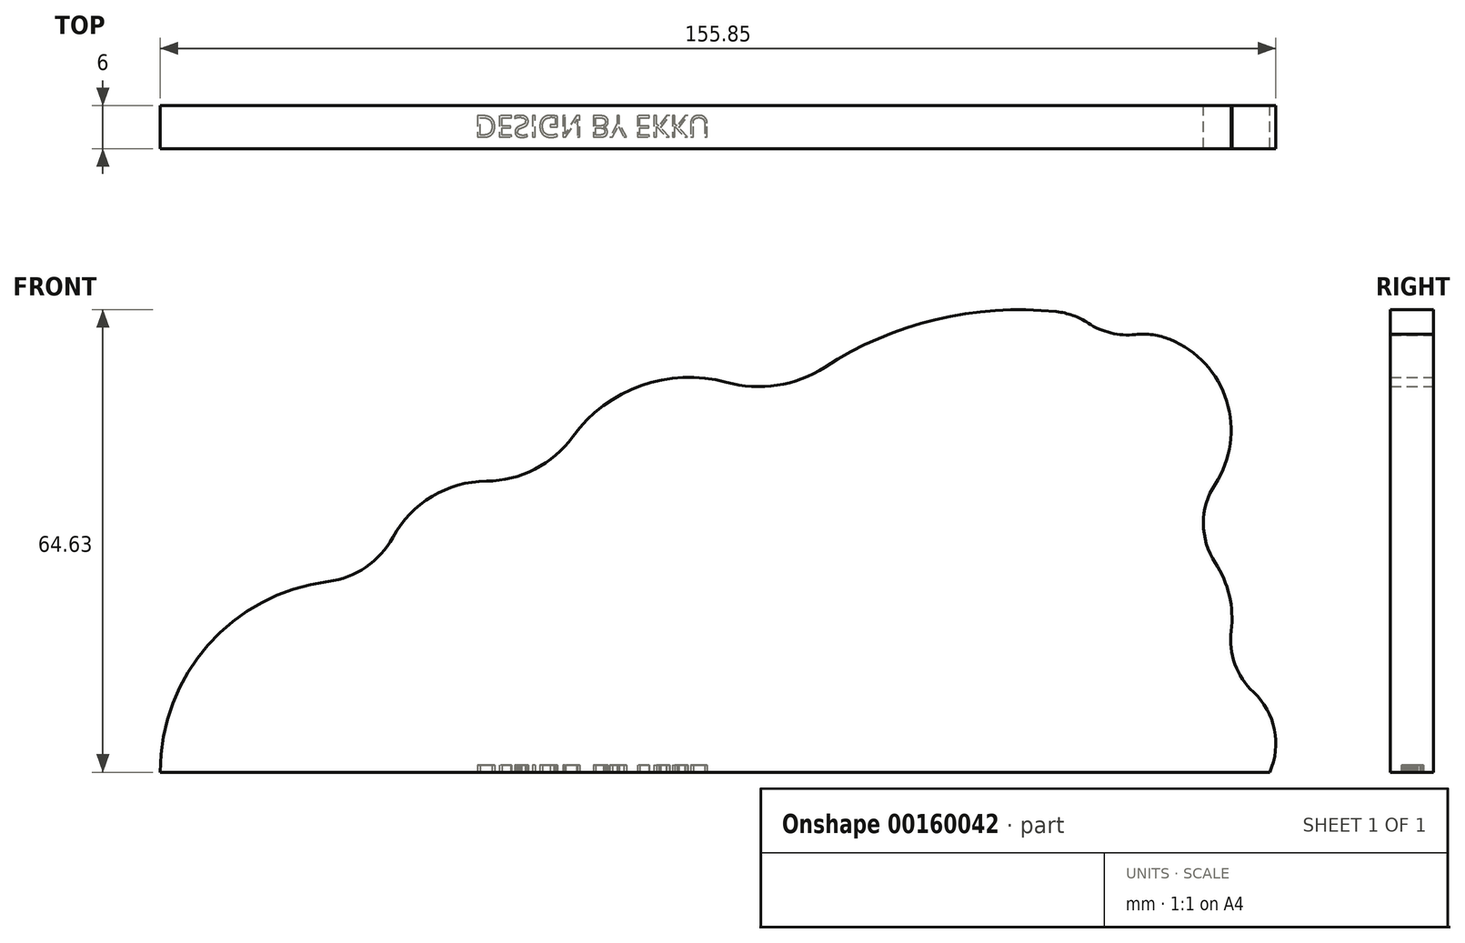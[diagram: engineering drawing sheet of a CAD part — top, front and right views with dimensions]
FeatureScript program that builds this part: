
annotation { "Feature Type Name" : "Feature", "Feature Type Description" : "" }
export const myFeature = defineFeature(function(context is Context, id is Id, definition is map)
    precondition{}
    {
        {
            var Q0;
            Q0=qCreatedBy(makeId("Front.planeOp"),FACE);
            var sketch = newSketch(context, id + "F0", { "sketchPlane" : qUnion([Q0])});
            skLineSegment(sketch, "E0", {"start": v(0, 0) * mm, "end": v(-155, 0) * mm});
            skArc(sketch, "E1", {"start": v(-109.41, 40.68) * mm, "mid": v(-117.02, 38.54) * mm, "end": v(-122.49, 32.84) * mm});
            skArc(sketch, "E2", {"start": v(-75.89, 54.47) * mm, "mid": v(-87.8, 54.04) * mm, "end": v(-97.36, 46.9) * mm});
            skArc(sketch, "E3", {"start": v(-29.82, 64.36) * mm, "mid": v(-46.66, 63.25) * mm, "end": v(-62.17, 56.6) * mm});
            skArc(sketch, "E4", {"start": v(-7.63, 40.26) * mm, "mid": v(-6, 51.86) * mm, "end": v(-13.93, 60.48) * mm});
            skArc(sketch, "E5", {"start": v(-5.38, 19.75) * mm, "mid": v(-5.64, 24.7) * mm, "end": v(-7.6, 29.26) * mm});
            skArc(sketch, "E6", {"start": v(0, 0) * mm, "mid": v(0.65, 5.96) * mm, "end": v(-2.28, 11.2) * mm});
            skArc(sketch, "E7", {"start": v(-17.22, 61.36) * mm, "mid": v(-91.43, 42.62) * mm, "end": v(-155, 0) * mm, "construction": true});
            skArc(sketch, "E8", {"start": v(-17.22, 61.36) * mm, "mid": v(-13.33, 29.35) * mm, "end": v(0, 0) * mm, "construction": true});
            skPoint(sketch, "E9.visualSharp", {"position": v(-143.88, 9.94) * mm});
            skPoint(sketch, "E10.visualSharp", {"position": v(-124.1, 23.21) * mm});
            skArc(sketch, "E10.filletArc", {"start": v(-131.52, 26.66) * mm, "mid": v(-126.26, 28.66) * mm, "end": v(-122.49, 32.84) * mm});
            skPoint(sketch, "E11.visualSharp", {"position": v(-100.93, 38.12) * mm});
            skArc(sketch, "E11.filletArc", {"start": v(-109.41, 40.68) * mm, "mid": v(-102.64, 42.34) * mm, "end": v(-97.36, 46.9) * mm});
            skPoint(sketch, "E12.visualSharp", {"position": v(-69.13, 51.16) * mm});
            skArc(sketch, "E12.filletArc", {"start": v(-75.89, 54.47) * mm, "mid": v(-68.8, 54.07) * mm, "end": v(-62.17, 56.6) * mm});
            skPoint(sketch, "E13.visualSharp", {"position": v(-14.7, 34.79) * mm});
            skArc(sketch, "E13.filletArc", {"start": v(-7.63, 40.26) * mm, "mid": v(-9.26, 34.76) * mm, "end": v(-7.6, 29.26) * mm});
            skPoint(sketch, "E14.visualSharp", {"position": v(-7.6, 13.75) * mm});
            skArc(sketch, "E14.filletArc", {"start": v(-5.38, 19.75) * mm, "mid": v(-4.86, 15.1) * mm, "end": v(-2.28, 11.2) * mm});
            skPoint(sketch, "E15.visualSharp", {"position": v(-17.22, 61.36) * mm});
            skArc(sketch, "E16", {"start": v(-25.34, 62.76) * mm, "mid": v(-22.2, 61.38) * mm, "end": v(-18.76, 61.16) * mm});
            skPoint(sketch, "E17.visualSharp", {"position": v(-26.83, 63.96) * mm});
            skArc(sketch, "E17.filletArc", {"start": v(-25.34, 62.76) * mm, "mid": v(-27.49, 63.83) * mm, "end": v(-29.82, 64.36) * mm});
            skPoint(sketch, "E18.visualSharp", {"position": v(-17.45, 61.39) * mm});
            skArc(sketch, "E18.filletArc", {"start": v(-13.93, 60.48) * mm, "mid": v(-16.3, 61.12) * mm, "end": v(-18.76, 61.16) * mm});
            skArc(sketch, "E19", {"start": v(-131.52, 26.66) * mm, "mid": v(-148.3, 17.76) * mm, "end": v(-155, 0) * mm});
            skPoint(sketch, "E20.center.orphan", {"position": v(-145, 0) * mm});
            skLineSegment(sketch, "E21", {"start": v(-155, 0) * mm, "end": v(-155, 26.27) * mm, "construction": true});
            skSolve(sketch);
        }
        {
            var Q0;
            Q0=qSketchRegion(id+"F0",true);
            extrude(context, id + "F1", {"entities" : qUnion([Q0]), "depth" : 6 * mm});
        }
        {
            var Q0;
            Q0=makeQuery(id+"F1.opExtrude","CAP_FACE",FACE,{"disambiguationData":[OSD([sQuery(id+"F0.wireOp",EDGE,"E0"),sQuery(id+"F0.wireOp",EDGE,"E20"),sQuery(id+"F0.wireOp",EDGE,"XMCz9Z54-D0iV-scBE-4L2D-qfeKU0g2q7XP"),sQuery(id+"F0.wireOp",EDGE,"E1"),sQuery(id+"F0.wireOp",EDGE,"E2"),sQuery(id+"F0.wireOp",EDGE,"E3"),sQuery(id+"F0.wireOp",EDGE,"E4"),sQuery(id+"F0.wireOp",EDGE,"E5"),sQuery(id+"F0.wireOp",EDGE,"E6"),sQuery(id+"F0.wireOp",EDGE,"E9.filletArc"),sQuery(id+"F0.wireOp",EDGE,"E10.filletArc"),sQuery(id+"F0.wireOp",EDGE,"E11.filletArc"),sQuery(id+"F0.wireOp",EDGE,"E12.filletArc"),sQuery(id+"F0.wireOp",EDGE,"E13.filletArc"),sQuery(id+"F0.wireOp",EDGE,"E14.filletArc"),sQuery(id+"F0.wireOp",EDGE,"E16"),sQuery(id+"F0.wireOp",EDGE,"E17.filletArc"),sQuery(id+"F0.wireOp",EDGE,"E18.filletArc")])],"isStart":false});
            var sketch = newSketch(context, id + "F2", { "sketchPlane" : qUnion([Q0])});
            skArc(sketch, "E22", {"start": v(0, 0) * mm, "mid": v(-0.66, -8.19) * mm, "end": v(3.96, -14.99) * mm});
            skSolve(sketch);
        }
        {
            var Q0;
            Q0=makeQuery(id+"F1.opExtrude","SWEPT_FACE",FACE,{"disambiguationData":[OSD([sQuery(id+"F0.wireOp",EDGE,"E0")])]});
            var sketch = newSketch(context, id + "F3", { "sketchPlane" : qUnion([Q0])});
            skArc(sketch, "E23", {"start": v(9, 6) * mm, "mid": v(4.26, 5.23) * mm, "end": v(0, 3) * mm});
            skLineSegment(sketch, "E24", {"start": v(-127.21, 3) * mm, "end": v(0, 3) * mm, "construction": true});
            skArc(sketch, "E25.MirrorCS", {"start": v(9, 0) * mm, "mid": v(4.26, 0.77) * mm, "end": v(0, 3) * mm});
            skLineSegment(sketch, "E26", {"start": v(9, 6) * mm, "end": v(9, 15) * mm});
            skLineSegment(sketch, "E27", {"start": v(9, 15) * mm, "end": v(-1, 15) * mm});
            skLineSegment(sketch, "E28", {"start": v(-1, 15) * mm, "end": v(-1, -9) * mm});
            skLineSegment(sketch, "E29", {"start": v(-1, -9) * mm, "end": v(9, -9) * mm});
            skLineSegment(sketch, "E30", {"start": v(9, 0) * mm, "end": v(9, -9) * mm});
            skSolve(sketch);
        }
        {
            var Q0;
            {var subQ0=sQuery(id+"F3.wireOp",EDGE,"E25.MirrorCS");Q0=makeQuery(id+"F3.imprint","IMPRINT",FACE,{"disambiguationData":[TD([[makeQuery(id+"F3.imprint","IMPRINT",EDGE,{"derivedFrom":subQ0}),1.0]])]});}
            var Q1;
            {var subQ0=sQuery(id+"F3.wireOp",EDGE,"E23");Q1=makeQuery(id+"F3.imprint","IMPRINT",FACE,{"disambiguationData":[TD([[makeQuery(id+"F3.imprint","IMPRINT",EDGE,{"derivedFrom":subQ0}),-1.0]])]});}
            var Q2;
            Q2=makeQuery(id+"F1.opExtrude","CAP_EDGE",EDGE,{"disambiguationData":[OSD([sQuery(id+"F0.wireOp",EDGE,"E20")])],"isStart":false});
            var Q3;
            Q3=makeQuery(id+"F1.opExtrude","CAP_EDGE",EDGE,{"disambiguationData":[OSD([sQuery(id+"F0.wireOp",EDGE,"E9.filletArc")])],"isStart":false});
            var Q4;
            Q4=makeQuery(id+"F1.opExtrude","CAP_EDGE",EDGE,{"disambiguationData":[OSD([sQuery(id+"F0.wireOp",EDGE,"XMCz9Z54-D0iV-scBE-4L2D-qfeKU0g2q7XP")])],"isStart":false});
            var Q5;
            Q5=makeQuery(id+"F1.opExtrude","CAP_EDGE",EDGE,{"disambiguationData":[OSD([sQuery(id+"F0.wireOp",EDGE,"E10.filletArc")])],"isStart":false});
            var Q6;
            Q6=makeQuery(id+"F1.opExtrude","CAP_EDGE",EDGE,{"disambiguationData":[OSD([sQuery(id+"F0.wireOp",EDGE,"E1")])],"isStart":false});
            var Q7;
            Q7=makeQuery(id+"F1.opExtrude","CAP_EDGE",EDGE,{"disambiguationData":[OSD([sQuery(id+"F0.wireOp",EDGE,"E11.filletArc")])],"isStart":false});
            var Q8;
            Q8=makeQuery(id+"F1.opExtrude","CAP_EDGE",EDGE,{"disambiguationData":[OSD([sQuery(id+"F0.wireOp",EDGE,"E2")])],"isStart":false});
            var Q9;
            Q9=makeQuery(id+"F1.opExtrude","CAP_EDGE",EDGE,{"disambiguationData":[OSD([sQuery(id+"F0.wireOp",EDGE,"E12.filletArc")])],"isStart":false});
            var Q10;
            Q10=makeQuery(id+"F1.opExtrude","CAP_EDGE",EDGE,{"disambiguationData":[OSD([sQuery(id+"F0.wireOp",EDGE,"E3")])],"isStart":false});
            var Q11;
            Q11=makeQuery(id+"F1.opExtrude","CAP_EDGE",EDGE,{"disambiguationData":[OSD([sQuery(id+"F0.wireOp",EDGE,"E4")])],"isStart":false});
            var Q12;
            Q12=makeQuery(id+"F1.opExtrude","CAP_EDGE",EDGE,{"disambiguationData":[OSD([sQuery(id+"F0.wireOp",EDGE,"E13.filletArc")])],"isStart":false});
            var Q13;
            Q13=makeQuery(id+"F1.opExtrude","CAP_EDGE",EDGE,{"disambiguationData":[OSD([sQuery(id+"F0.wireOp",EDGE,"E5")])],"isStart":false});
            var Q14;
            Q14=makeQuery(id+"F1.opExtrude","CAP_EDGE",EDGE,{"disambiguationData":[OSD([sQuery(id+"F0.wireOp",EDGE,"E14.filletArc")])],"isStart":false});
            var Q15;
            Q15=makeQuery(id+"F1.opExtrude","CAP_EDGE",EDGE,{"disambiguationData":[OSD([sQuery(id+"F0.wireOp",EDGE,"E6")])],"isStart":false});
            var Q16;
            Q16=makeQuery(id+"F1.opExtrude","CAP_EDGE",EDGE,{"disambiguationData":[OSD([sQuery(id+"F0.wireOp",EDGE,"E17.filletArc")])],"isStart":false});
            var Q17;
            Q17=makeQuery(id+"F1.opExtrude","CAP_EDGE",EDGE,{"disambiguationData":[OSD([sQuery(id+"F0.wireOp",EDGE,"E16")])],"isStart":false});
            var Q18;
            Q18=makeQuery(id+"F1.opExtrude","CAP_EDGE",EDGE,{"disambiguationData":[OSD([sQuery(id+"F0.wireOp",EDGE,"E18.filletArc")])],"isStart":false});
            var Q19;
            Q19=sQuery(id+"F2.wireOp",EDGE,"E22");
            sweep(context, id + "F4", {"operationType" : NewBodyOperationType.REMOVE, "profiles" : qUnion([Q0, Q1]), "path" : qUnion([Q2, Q3, Q4, Q5, Q6, Q7, Q8, Q9, Q10, Q11, Q12, Q13, Q14, Q15, Q16, Q17, Q18, Q19])});
        }
        {
            var Q0;
            Q0=makeQuery(id+"F1.opExtrude","SWEPT_FACE",FACE,{"disambiguationData":[OSD([sQuery(id+"F0.wireOp",EDGE,"E0")])]});
            var sketch = newSketch(context, id + "F5", { "sketchPlane" : qUnion([Q0])});
            skText(sketch, "E31", { "text": "DESIGN BY EKKU", "fontName": "OpenSans-Regular.ttf"});
            const initialGuessF5  = {"E31": [-0.11107, 0.0014, 1, 0, 0.00302]};
            skSetInitialGuess(sketch, initialGuessF5);
            skSolve(sketch);
        }
        {
            var Q0;
            Q0=qSketchRegion(id+"F5",true);
            extrude(context, id + "F6", {"entities" : qUnion([Q0]), "operationType" : NewBodyOperationType.REMOVE, "oppositeDirection" : true, "depth" : 1 * mm});
        }
    });
